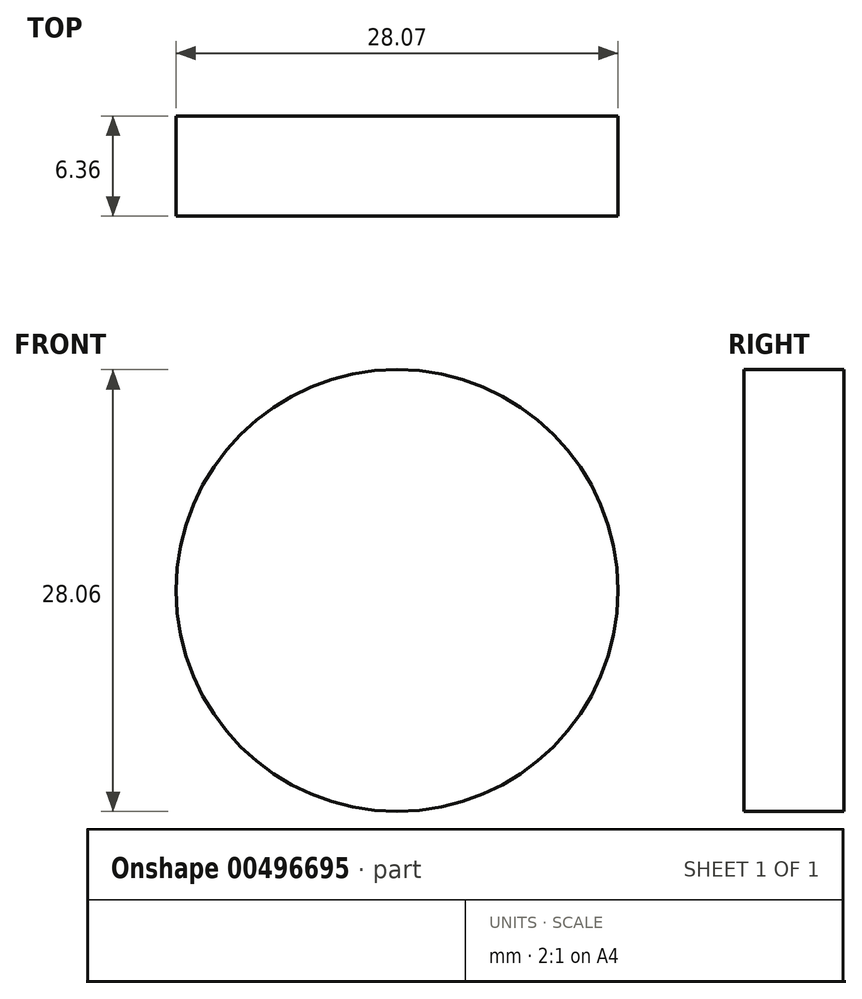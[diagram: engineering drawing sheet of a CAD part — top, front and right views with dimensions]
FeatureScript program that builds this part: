
annotation { "Feature Type Name" : "Feature", "Feature Type Description" : "" }
export const myFeature = defineFeature(function(context is Context, id is Id, definition is map)
    precondition{}
    {
        {
            var Q0;
            Q0=qCreatedBy(makeId("Front.planeOp"),FACE);
            var sketch = newSketch(context, id + "F0", { "sketchPlane" : qUnion([Q0])});
            skCircle(sketch, "E0", {"center": v(-29.5, -22.15) * mm, "radius": 14.03 * mm});
            skSolve(sketch);
        }
        {
            var Q0;
            Q0=makeQuery(id+"F0.imprint","IMPRINT",FACE,{"disambiguationData":[TD([[makeQuery(id+"F0.imprint","IMPRINT",EDGE,{"derivedFrom":sQuery(id+"F0.wireOp",EDGE,"E0")}),1.0]])]});
            extrude(context, id + "F1", {"entities" : qUnion([Q0]), "endBound" : BoundingType.SYMMETRIC, "depth" : 6.35 * mm});
        }
    });
